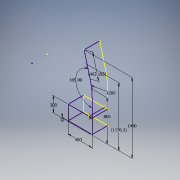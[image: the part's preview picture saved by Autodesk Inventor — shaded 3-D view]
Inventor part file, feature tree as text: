
AUTODESK INVENTOR PART (.ipt)
format: ipt  version: 2016 (Build 200138000, 138)  size: 105,472 bytes
history: native  units: mm
features: sketch x5, plane x2, mirror x1
ambient origin geometry x8: Origin, YZ Plane, XZ Plane, XY Plane, X Axis, Y Axis, Z Axis, Center Point
feature tree (8):
  plane  "Work Plane1"
  mirror  "Mirror1"
  sketch  "Sketch1"  dims[d0=155.0mm]
  sketch  "Sketch2"  dims[d2=1400.0mm d3=165.0deg d4=800.0mm d5=1200.0mm d6=480.0mm d7=300.0mm d8=15.0mm d9=1176.299929mm d10=463.182711mm d11=60.0mm d12=407.0mm]
  sketch  "3D Sketch1"
  sketch  "3D Sketch2"
  sketch  "3D Sketch3"
  plane  "Work Plane2"
